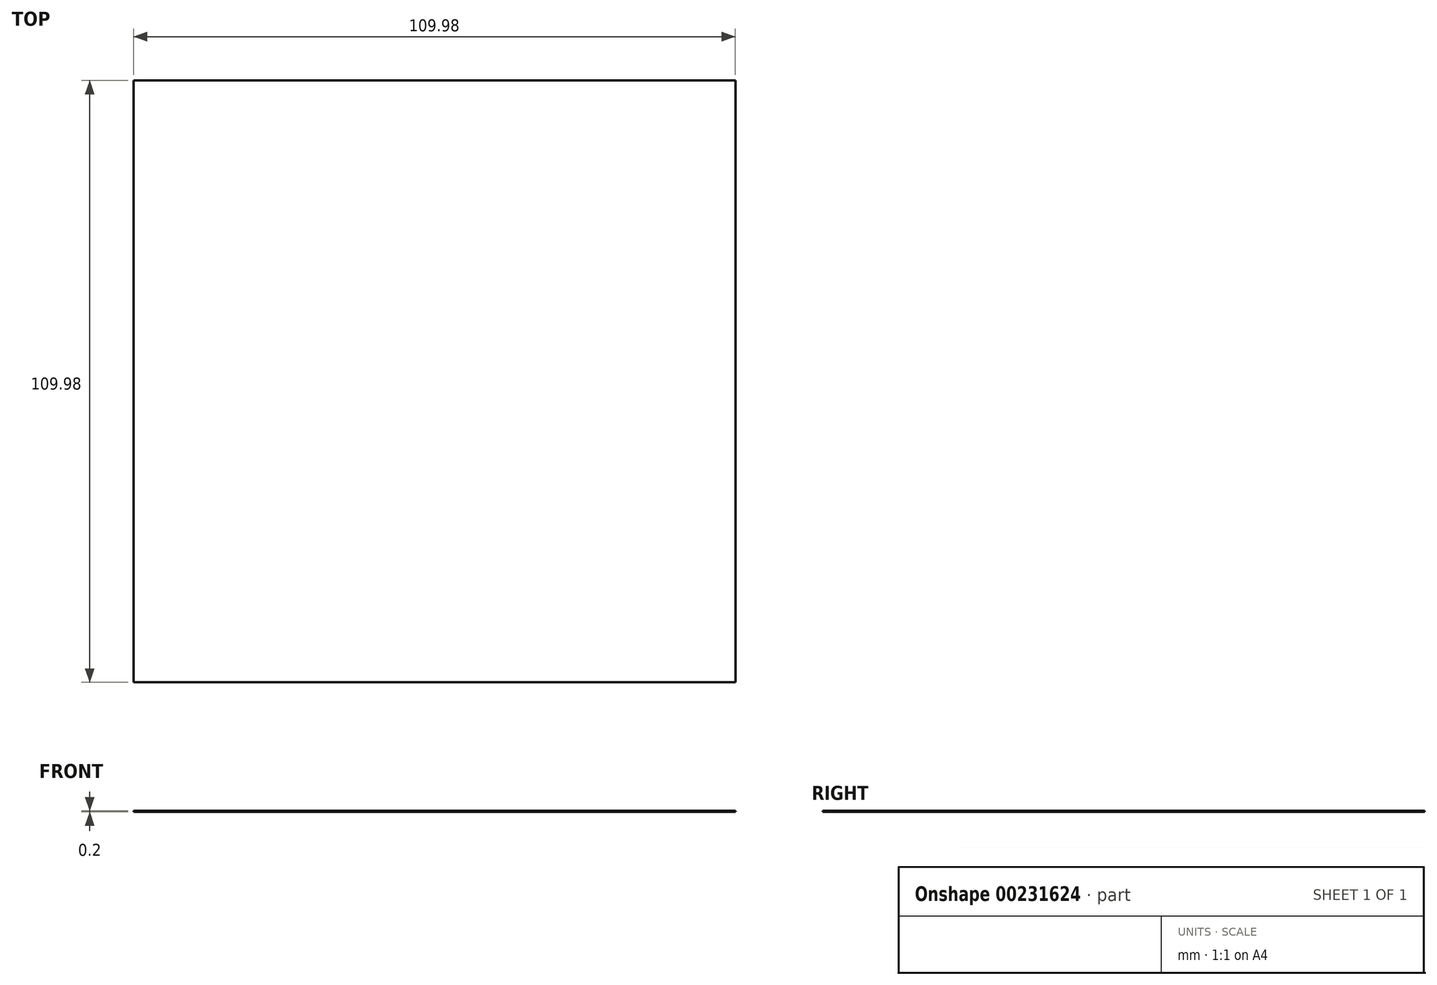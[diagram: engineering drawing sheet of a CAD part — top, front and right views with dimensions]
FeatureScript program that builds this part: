
annotation { "Feature Type Name" : "Feature", "Feature Type Description" : "" }
export const myFeature = defineFeature(function(context is Context, id is Id, definition is map)
    precondition{}
    {
        {
            var Q0;
            Q0=qCreatedBy(makeId("Top.planeOp"),FACE);
            var sketch = newSketch(context, id + "F0", { "sketchPlane" : qUnion([Q0])});
            skLineSegment(sketch, "E0.bottom", {"start": v(55, 55) * mm, "end": v(-55, 55) * mm});
            skLineSegment(sketch, "E0.top", {"start": v(55, -55) * mm, "end": v(-55, -55) * mm});
            skLineSegment(sketch, "E0.left", {"start": v(55, 55) * mm, "end": v(55, -55) * mm});
            skLineSegment(sketch, "E0.right", {"start": v(-55, 55) * mm, "end": v(-55, -55) * mm});
            skPoint(sketch, "E0.middle", {"position": v(0, 0) * mm});
            skSolve(sketch);
        }
        {
            var Q0;
            Q0=makeQuery(id+"F0.imprint","IMPRINT",FACE,{"disambiguationData":[TD([[makeQuery(id+"F0.imprint","IMPRINT",EDGE,{"derivedFrom":sQuery(id+"F0.wireOp",EDGE,"E0.bottom")}),1.0]])]});
            extrude(context, id + "F1", {"entities" : qUnion([Q0]), "depth" : 0.2 * mm});
        }
    });
